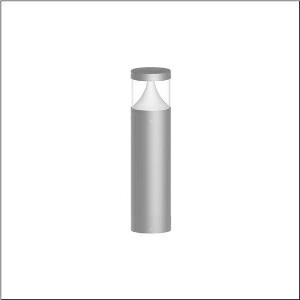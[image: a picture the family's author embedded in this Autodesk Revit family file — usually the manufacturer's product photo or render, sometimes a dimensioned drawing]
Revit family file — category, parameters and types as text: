
# Revit family: cl_31_poller_60_5cl434603
name_source: partatom
category: Lighting Fixtures
units: mm (PartAtom-declared; Revit-internal decimal feet)

## family parameters
Cut with Voids When Loaded = No
Host = Face
Light Source = No
Part Type = Normal
Room Calculation Point = No
Round Connector Dimension = Use Diameter
Shared = No

## types (1)
- --- (1 x LED, 1500 lm, 14 W, 3000K)
    Apparent Load = 14 VA
    CIE Flux Codes = 19 66 88 92 100
    Color Rendering = 80
    Color Temperature = 3000K
    Default Elevation = 1800 mm
    Description = CL 31 Bollard 60, bollard luminaire, primary light control with lens, of PC, primary optical cover: cover panel, of PC, transparent, secondary light control with reflector, of PC, primary light characteristic: asymmetric, LED, rated luminous flux: 1.500lm, luminous efficacy: 107lm/W, light colour: 830, colour temperature: 3000K, control gear: ECG DALI, with terminal, 5-pole, max. 2.5mm², mains connection: 220..240V, AC, 50/60Hz, rated input power: 14W, luminaire housing, of aluminium, powder-coated, Siteco® metallic grey, diameter: 170mm, height: 600mm, protection rating (complete): IP65, insulation class (complete): insulation class I (protective earthing), certification: CE, ENEC, impact resistance: IK10, permissible operating ambient temperature for outdoor applications: -20..+50°C, packaging unit: 1 piece
    Height = 200 mm  [stored 0.656168 ft]
    Lamp = 1 x LED
    Lamp Light Flux = 1500 lm
    Lamp Power = 14 W
    Lamp count = 1
    Length = 170 mm  [stored 0.557743 ft]
    Luminous efficacy = 107 lm/W
    Manufacturer = Siteco
    ModVariant = No
    Model = 5CL434603
    Mounting Place = Floor
    Mounting Type = Freestanding
    Number of Poles = 1
    OnlyDefault = Yes
    Power Factor = 1
    Product Name = CL 31 Poller 60
    Product group = bollard luminaire
    ProductGroupID = 1304
    Protection Class = Protection class I
    Protection Degree = IP 65
    RLX_Detail_Level = 1
    RLX_Emergency_Light_Flux = 0 lm
    RLX_Emergency_Type = 0
    RLX_Emergency_Type_DB = No
    RlxData = <blob elided: 63797 chars, md5=3366a22e>
    Socket = socket
    Standby Power = 0 W
    System Light Flux = 1500 lm
    System Power = 14 W
    Type Comments = factory setting: luminous flux: 100 % | dim-lin: 254 | 350 mA
    Type Image = l_1006903.jpg
    URL = http://relux.com
    VarID = @adj_148373
    Voltage = 0 V
    Weight = 0.00 kg
    Width = 0 mm  [stored 0 ft]

note: [stored X ft] marks values corroborated as IEEE doubles in the binary element streams (Revit-internal decimal feet)

## geometry (parser evidence)
native form markers: Blend x4, Sweep x13
no freeform markers — native parametric forms only
